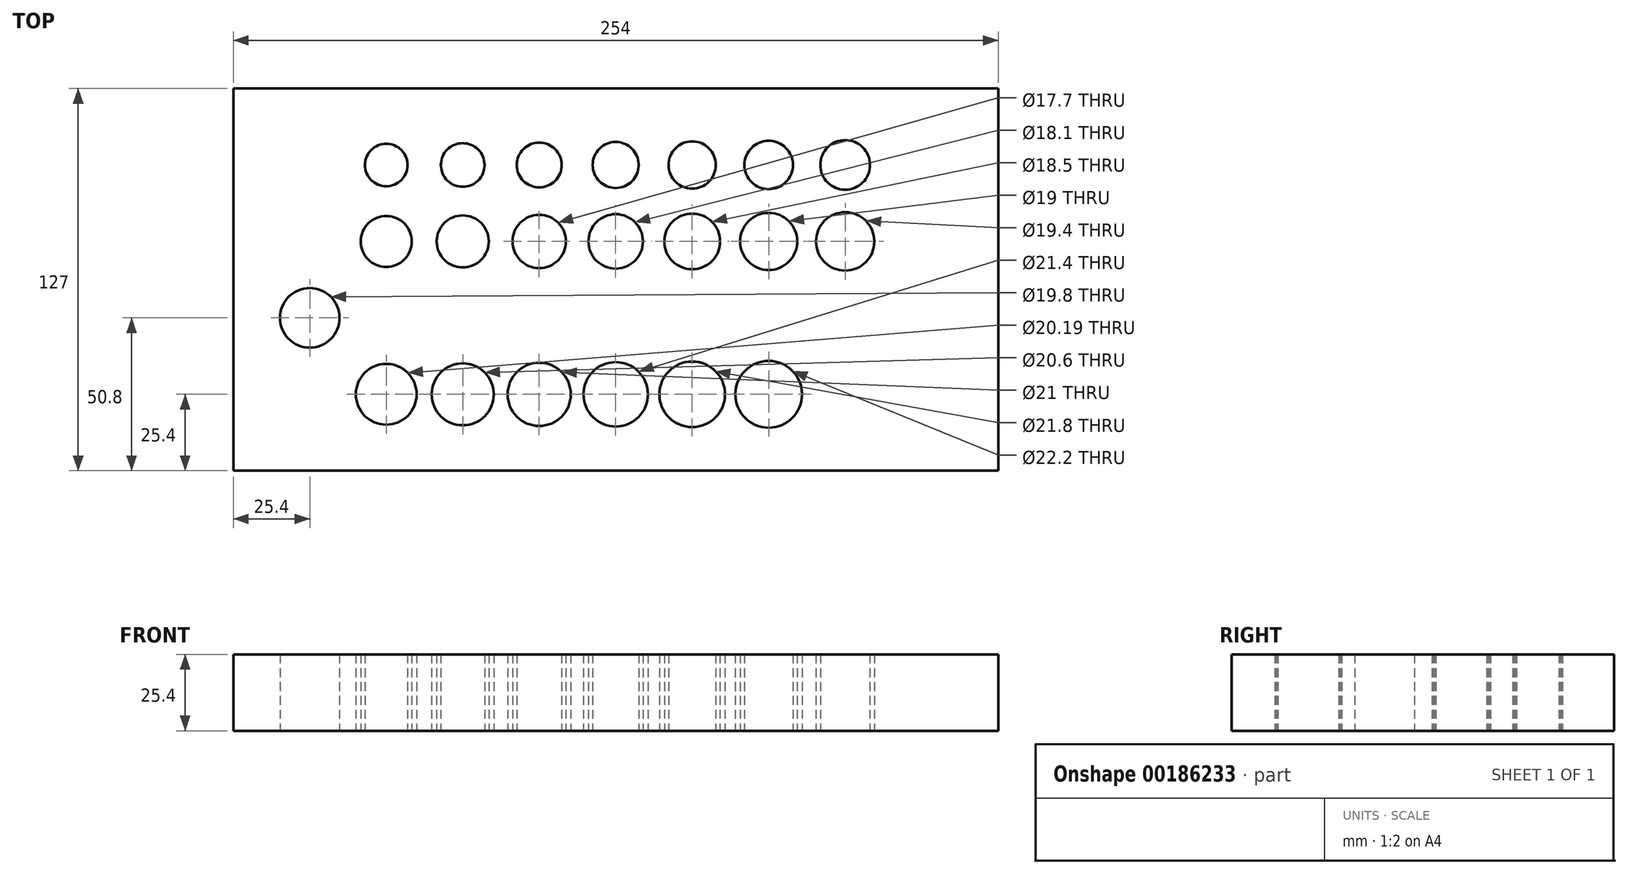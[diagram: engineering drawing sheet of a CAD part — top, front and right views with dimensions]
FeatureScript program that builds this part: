
annotation { "Feature Type Name" : "Feature", "Feature Type Description" : "" }
export const myFeature = defineFeature(function(context is Context, id is Id, definition is map)
    precondition{}
    {
        {
            var Q0;
            Q0=qCreatedBy(makeId("Top.planeOp"),FACE);
            var sketch = newSketch(context, id + "F0", { "sketchPlane" : qUnion([Q0])});
            skLineSegment(sketch, "E0.bottom", {"start": v(-127, 63.5) * mm, "end": v(127, 63.5) * mm});
            skLineSegment(sketch, "E0.top", {"start": v(-127, -63.5) * mm, "end": v(127, -63.5) * mm});
            skLineSegment(sketch, "E0.left", {"start": v(-127, 63.5) * mm, "end": v(-127, -63.5) * mm});
            skLineSegment(sketch, "E0.right", {"start": v(127, 63.5) * mm, "end": v(127, -63.5) * mm});
            skPoint(sketch, "E0.middle", {"position": v(0, 0) * mm});
            skPoint(sketch, "E1", {"position": v(-127, 38.1) * mm});
            skPoint(sketch, "E2", {"position": v(-127, 12.7) * mm});
            skPoint(sketch, "E3", {"position": v(-127, -12.7) * mm});
            skPoint(sketch, "E4", {"position": v(-127, -38.1) * mm});
            skPoint(sketch, "E5", {"position": v(-101.6, 63.5) * mm});
            skPoint(sketch, "E6", {"position": v(-76.2, 63.5) * mm});
            skPoint(sketch, "E7", {"position": v(-50.8, 63.5) * mm});
            skPoint(sketch, "E8", {"position": v(-25.4, 63.5) * mm});
            skPoint(sketch, "E9", {"position": v(0, 63.5) * mm});
            skPoint(sketch, "E10", {"position": v(25.4, 63.5) * mm});
            skPoint(sketch, "E11", {"position": v(50.8, 63.5) * mm});
            skPoint(sketch, "E12", {"position": v(76.2, 63.5) * mm});
            skPoint(sketch, "E13", {"position": v(101.6, 63.5) * mm});
            skPoint(sketch, "E14", {"position": v(-101.6, 38.1) * mm});
            skPoint(sketch, "E15", {"position": v(-76.2, 38.1) * mm});
            skPoint(sketch, "E16", {"position": v(-50.8, 38.1) * mm});
            skPoint(sketch, "E17", {"position": v(-25.4, 38.1) * mm});
            skPoint(sketch, "E18", {"position": v(0, 38.1) * mm});
            skPoint(sketch, "E19", {"position": v(25.4, 38.1) * mm});
            skPoint(sketch, "E20", {"position": v(50.8, 38.1) * mm});
            skPoint(sketch, "E21", {"position": v(76.2, 38.1) * mm});
            skPoint(sketch, "E22", {"position": v(101.6, 38.1) * mm});
            skPoint(sketch, "E23", {"position": v(-101.6, 12.7) * mm});
            skPoint(sketch, "E24", {"position": v(-76.2, 12.7) * mm});
            skPoint(sketch, "E25", {"position": v(-50.8, 12.7) * mm});
            skPoint(sketch, "E26", {"position": v(-25.4, 12.7) * mm});
            skPoint(sketch, "E27", {"position": v(0, 12.7) * mm});
            skPoint(sketch, "E28", {"position": v(25.4, 12.7) * mm});
            skPoint(sketch, "E29", {"position": v(50.8, 12.7) * mm});
            skPoint(sketch, "E30", {"position": v(76.2, 12.7) * mm});
            skPoint(sketch, "E31", {"position": v(101.6, 12.7) * mm});
            skPoint(sketch, "E32", {"position": v(-101.6, -12.7) * mm});
            skPoint(sketch, "E33", {"position": v(-76.2, -12.7) * mm});
            skPoint(sketch, "E34", {"position": v(-50.8, -12.7) * mm});
            skPoint(sketch, "E35", {"position": v(-25.4, -12.7) * mm});
            skPoint(sketch, "E36", {"position": v(0, -12.7) * mm});
            skPoint(sketch, "E37", {"position": v(25.4, -12.7) * mm});
            skPoint(sketch, "E38", {"position": v(50.8, -12.7) * mm});
            skPoint(sketch, "E39", {"position": v(76.2, -12.7) * mm});
            skPoint(sketch, "E40", {"position": v(101.6, -12.7) * mm});
            skPoint(sketch, "E41", {"position": v(-101.6, -38.1) * mm});
            skPoint(sketch, "E42", {"position": v(-76.2, -38.1) * mm});
            skPoint(sketch, "E43", {"position": v(-50.8, -38.1) * mm});
            skPoint(sketch, "E44", {"position": v(-25.4, -38.1) * mm});
            skPoint(sketch, "E45", {"position": v(0, -38.1) * mm});
            skPoint(sketch, "E46", {"position": v(25.4, -38.1) * mm});
            skPoint(sketch, "E47", {"position": v(50.8, -38.1) * mm});
            skPoint(sketch, "E48", {"position": v(76.2, -38.1) * mm});
            skPoint(sketch, "E49", {"position": v(101.6, -38.1) * mm});
            skCircle(sketch, "E50", {"center": v(-76.2, 38.1) * mm, "radius": 7.05 * mm});
            skCircle(sketch, "E51", {"center": v(-50.8, 38.1) * mm, "radius": 7.25 * mm});
            skCircle(sketch, "E52", {"center": v(-25.4, 38.1) * mm, "radius": 7.45 * mm});
            skCircle(sketch, "E53", {"center": v(0, 38.1) * mm, "radius": 7.65 * mm});
            skCircle(sketch, "E54", {"center": v(25.4, 38.1) * mm, "radius": 7.85 * mm});
            skCircle(sketch, "E55", {"center": v(50.8, 38.1) * mm, "radius": 8.05 * mm});
            skCircle(sketch, "E56", {"center": v(76.2, 38.1) * mm, "radius": 8.25 * mm});
            skCircle(sketch, "E57", {"center": v(-76.2, 12.7) * mm, "radius": 8.45 * mm});
            skCircle(sketch, "E58", {"center": v(-50.8, 12.7) * mm, "radius": 8.65 * mm});
            skCircle(sketch, "E59", {"center": v(-25.4, 12.7) * mm, "radius": 8.85 * mm});
            skCircle(sketch, "E60", {"center": v(0, 12.7) * mm, "radius": 9.05 * mm});
            skCircle(sketch, "E61", {"center": v(25.4, 12.7) * mm, "radius": 9.25 * mm});
            skCircle(sketch, "E62", {"center": v(50.8, 12.7) * mm, "radius": 9.5 * mm});
            skCircle(sketch, "E63", {"center": v(76.2, 12.7) * mm, "radius": 9.7 * mm});
            skCircle(sketch, "E64", {"center": v(0, -38.1) * mm, "radius": 10.7 * mm});
            skLineSegment(sketch, "E65", {"start": v(-76.2, 38.1) * mm, "end": v(-76.2, 50.06) * mm});
            skLineSegment(sketch, "E66.top", {"start": v(-71.64, 52.52) * mm, "end": v(-80.76, 52.52) * mm});
            skLineSegment(sketch, "E66.left", {"start": v(-71.64, 47.61) * mm, "end": v(-71.64, 52.52) * mm});
            skLineSegment(sketch, "E66.right", {"start": v(-80.76, 47.61) * mm, "end": v(-80.76, 52.52) * mm});
            skPoint(sketch, "E66.middle", {"position": v(-76.2, 50.06) * mm});
            skLineSegment(sketch, "E67.0.1.0", {"start": v(-71.64, 28.13) * mm, "end": v(-80.76, 28.13) * mm});
            skLineSegment(sketch, "E67.0.1.1", {"start": v(-71.64, 23.23) * mm, "end": v(-71.64, 28.13) * mm});
            skLineSegment(sketch, "E67.0.1.2", {"start": v(-71.64, 23.23) * mm, "end": v(-80.76, 23.23) * mm});
            skLineSegment(sketch, "E67.0.1.3", {"start": v(-80.76, 23.23) * mm, "end": v(-80.76, 28.13) * mm});
            skLineSegment(sketch, "E67.1.0.0", {"start": v(-46.24, 52.52) * mm, "end": v(-55.36, 52.52) * mm});
            skLineSegment(sketch, "E67.1.0.1", {"start": v(-46.24, 47.61) * mm, "end": v(-46.24, 52.52) * mm});
            skLineSegment(sketch, "E67.1.0.2", {"start": v(-46.24, 47.61) * mm, "end": v(-55.36, 47.61) * mm});
            skLineSegment(sketch, "E67.1.0.3", {"start": v(-55.36, 47.61) * mm, "end": v(-55.36, 52.52) * mm});
            skLineSegment(sketch, "E67.1.1.0", {"start": v(-46.24, 28.13) * mm, "end": v(-55.36, 28.13) * mm});
            skLineSegment(sketch, "E67.1.1.1", {"start": v(-46.24, 23.23) * mm, "end": v(-46.24, 28.13) * mm});
            skLineSegment(sketch, "E67.1.1.2", {"start": v(-46.24, 23.23) * mm, "end": v(-55.36, 23.23) * mm});
            skLineSegment(sketch, "E67.1.1.3", {"start": v(-55.36, 23.23) * mm, "end": v(-55.36, 28.13) * mm});
            skLineSegment(sketch, "E67.2.0.0", {"start": v(-20.84, 52.52) * mm, "end": v(-29.96, 52.52) * mm});
            skLineSegment(sketch, "E67.2.0.1", {"start": v(-20.84, 47.61) * mm, "end": v(-20.84, 52.52) * mm});
            skLineSegment(sketch, "E67.2.0.2", {"start": v(-20.84, 47.61) * mm, "end": v(-29.96, 47.61) * mm});
            skLineSegment(sketch, "E67.2.0.3", {"start": v(-29.96, 47.61) * mm, "end": v(-29.96, 52.52) * mm});
            skLineSegment(sketch, "E67.2.1.0", {"start": v(-20.84, 28.13) * mm, "end": v(-29.96, 28.13) * mm});
            skLineSegment(sketch, "E67.2.1.1", {"start": v(-20.84, 23.23) * mm, "end": v(-20.84, 28.13) * mm});
            skLineSegment(sketch, "E67.2.1.2", {"start": v(-20.84, 23.23) * mm, "end": v(-29.96, 23.23) * mm});
            skLineSegment(sketch, "E67.2.1.3", {"start": v(-29.96, 23.23) * mm, "end": v(-29.96, 28.13) * mm});
            skLineSegment(sketch, "E67.3.0.0", {"start": v(4.56, 52.52) * mm, "end": v(-4.56, 52.52) * mm});
            skLineSegment(sketch, "E67.3.0.1", {"start": v(4.56, 47.61) * mm, "end": v(4.56, 52.52) * mm});
            skLineSegment(sketch, "E67.3.0.2", {"start": v(4.56, 47.61) * mm, "end": v(-4.56, 47.61) * mm});
            skLineSegment(sketch, "E67.3.0.3", {"start": v(-4.56, 47.61) * mm, "end": v(-4.56, 52.52) * mm});
            skLineSegment(sketch, "E67.3.1.0", {"start": v(4.56, 28.13) * mm, "end": v(-4.56, 28.13) * mm});
            skLineSegment(sketch, "E67.3.1.1", {"start": v(4.56, 23.23) * mm, "end": v(4.56, 28.13) * mm});
            skLineSegment(sketch, "E67.3.1.2", {"start": v(4.56, 23.23) * mm, "end": v(-4.56, 23.23) * mm});
            skLineSegment(sketch, "E67.3.1.3", {"start": v(-4.56, 23.23) * mm, "end": v(-4.56, 28.13) * mm});
            skLineSegment(sketch, "E67.4.0.0", {"start": v(29.96, 52.52) * mm, "end": v(20.84, 52.52) * mm});
            skLineSegment(sketch, "E67.4.0.1", {"start": v(29.96, 47.61) * mm, "end": v(29.96, 52.52) * mm});
            skLineSegment(sketch, "E67.4.0.2", {"start": v(29.96, 47.61) * mm, "end": v(20.84, 47.61) * mm});
            skLineSegment(sketch, "E67.4.0.3", {"start": v(20.84, 47.61) * mm, "end": v(20.84, 52.52) * mm});
            skLineSegment(sketch, "E67.4.1.0", {"start": v(29.96, 28.13) * mm, "end": v(20.84, 28.13) * mm});
            skLineSegment(sketch, "E67.4.1.1", {"start": v(29.96, 23.23) * mm, "end": v(29.96, 28.13) * mm});
            skLineSegment(sketch, "E67.4.1.2", {"start": v(29.96, 23.23) * mm, "end": v(20.84, 23.23) * mm});
            skLineSegment(sketch, "E67.4.1.3", {"start": v(20.84, 23.23) * mm, "end": v(20.84, 28.13) * mm});
            skLineSegment(sketch, "E67.5.0.0", {"start": v(55.36, 52.52) * mm, "end": v(46.24, 52.52) * mm});
            skLineSegment(sketch, "E67.5.0.1", {"start": v(55.36, 47.61) * mm, "end": v(55.36, 52.52) * mm});
            skLineSegment(sketch, "E67.5.0.2", {"start": v(55.36, 47.61) * mm, "end": v(46.24, 47.61) * mm});
            skLineSegment(sketch, "E67.5.0.3", {"start": v(46.24, 47.61) * mm, "end": v(46.24, 52.52) * mm});
            skLineSegment(sketch, "E67.5.1.0", {"start": v(55.36, 28.13) * mm, "end": v(46.24, 28.13) * mm});
            skLineSegment(sketch, "E67.5.1.1", {"start": v(55.36, 23.23) * mm, "end": v(55.36, 28.13) * mm});
            skLineSegment(sketch, "E67.5.1.2", {"start": v(55.36, 23.23) * mm, "end": v(46.24, 23.23) * mm});
            skLineSegment(sketch, "E67.5.1.3", {"start": v(46.24, 23.23) * mm, "end": v(46.24, 28.13) * mm});
            skLineSegment(sketch, "E67.6.0.0", {"start": v(80.76, 52.52) * mm, "end": v(71.64, 52.52) * mm});
            skLineSegment(sketch, "E67.6.0.1", {"start": v(80.76, 47.61) * mm, "end": v(80.76, 52.52) * mm});
            skLineSegment(sketch, "E67.6.0.2", {"start": v(80.76, 47.61) * mm, "end": v(71.64, 47.61) * mm});
            skLineSegment(sketch, "E67.6.0.3", {"start": v(71.64, 47.61) * mm, "end": v(71.64, 52.52) * mm});
            skLineSegment(sketch, "E67.6.1.0", {"start": v(80.76, 28.13) * mm, "end": v(71.64, 28.13) * mm});
            skLineSegment(sketch, "E67.6.1.1", {"start": v(80.76, 23.23) * mm, "end": v(80.76, 28.13) * mm});
            skLineSegment(sketch, "E67.6.1.2", {"start": v(80.76, 23.23) * mm, "end": v(71.64, 23.23) * mm});
            skLineSegment(sketch, "E67.6.1.3", {"start": v(71.64, 23.23) * mm, "end": v(71.64, 28.13) * mm});
            skLineSegment(sketch, "E67.7.0.0", {"start": v(106.16, 52.52) * mm, "end": v(97.04, 52.52) * mm});
            skLineSegment(sketch, "E67.7.0.1", {"start": v(106.16, 47.61) * mm, "end": v(106.16, 52.52) * mm});
            skLineSegment(sketch, "E67.7.0.2", {"start": v(106.16, 47.61) * mm, "end": v(97.04, 47.61) * mm});
            skLineSegment(sketch, "E67.7.0.3", {"start": v(97.04, 47.61) * mm, "end": v(97.04, 52.52) * mm});
            skLineSegment(sketch, "E67.7.1.0", {"start": v(106.16, 28.13) * mm, "end": v(97.04, 28.13) * mm});
            skLineSegment(sketch, "E67.7.1.1", {"start": v(106.16, 23.23) * mm, "end": v(106.16, 28.13) * mm});
            skLineSegment(sketch, "E67.7.1.2", {"start": v(106.16, 23.23) * mm, "end": v(97.04, 23.23) * mm});
            skLineSegment(sketch, "E67.7.1.3", {"start": v(97.04, 23.23) * mm, "end": v(97.04, 28.13) * mm});
            skLineSegment(sketch, "E67.8.0.0", {"start": v(131.56, 52.52) * mm, "end": v(122.44, 52.52) * mm});
            skLineSegment(sketch, "E67.8.0.1", {"start": v(131.56, 47.61) * mm, "end": v(131.56, 52.52) * mm});
            skLineSegment(sketch, "E67.8.0.2", {"start": v(131.56, 47.61) * mm, "end": v(122.44, 47.61) * mm});
            skLineSegment(sketch, "E67.8.0.3", {"start": v(122.44, 47.61) * mm, "end": v(122.44, 52.52) * mm});
            skLineSegment(sketch, "E67.8.1.0", {"start": v(131.56, 28.13) * mm, "end": v(122.44, 28.13) * mm});
            skLineSegment(sketch, "E67.8.1.1", {"start": v(131.56, 23.23) * mm, "end": v(131.56, 28.13) * mm});
            skLineSegment(sketch, "E67.8.1.2", {"start": v(131.56, 23.23) * mm, "end": v(122.44, 23.23) * mm});
            skLineSegment(sketch, "E67.8.1.3", {"start": v(122.44, 23.23) * mm, "end": v(122.44, 28.13) * mm});
            skLineSegment(sketch, "E67.direction1", {"start": v(-80.76, 52.52) * mm, "end": v(-55.36, 52.52) * mm, "construction": true});
            skLineSegment(sketch, "E67.direction2", {"start": v(-80.76, 52.52) * mm, "end": v(-80.76, 28.13) * mm, "construction": true});
            skCircle(sketch, "E68", {"center": v(-101.6, -12.7) * mm, "radius": 9.9 * mm});
            skCircle(sketch, "E69", {"center": v(-76.2, -38.1) * mm, "radius": 10.1 * mm});
            skCircle(sketch, "E70", {"center": v(-50.8, -38.1) * mm, "radius": 10.3 * mm});
            skCircle(sketch, "E71", {"center": v(-25.4, -38.1) * mm, "radius": 10.5 * mm});
            skCircle(sketch, "E72", {"center": v(25.4, -38.1) * mm, "radius": 10.9 * mm});
            skCircle(sketch, "E73", {"center": v(50.8, -38.1) * mm, "radius": 11.1 * mm});
            skCircle(sketch, "E74", {"center": v(101.6, -38.1) * mm, "radius": 23.67 * mm});
            skLineSegment(sketch, "E75.0.1.0", {"start": v(-95.91, 0.1) * mm, "end": v(-105.03, 0.1) * mm});
            skLineSegment(sketch, "E75.0.1.1", {"start": v(-95.91, 0.1) * mm, "end": v(-95.91, 5) * mm});
            skLineSegment(sketch, "E75.0.1.2", {"start": v(-95.91, 5) * mm, "end": v(-105.03, 5) * mm});
            skLineSegment(sketch, "E75.direction1", {"start": v(-80.76, 23.23) * mm, "end": v(-55.36, 23.23) * mm, "construction": true});
            skLineSegment(sketch, "E75.direction2", {"start": v(-80.76, 23.23) * mm, "end": v(-105.03, 0.1) * mm, "construction": true});
            skLineSegment(sketch, "E76.0.1.0", {"start": v(-71.64, -19.37) * mm, "end": v(-80.76, -19.37) * mm});
            skLineSegment(sketch, "E76.0.1.1", {"start": v(-80.76, -24.27) * mm, "end": v(-80.76, -19.37) * mm});
            skLineSegment(sketch, "E76.0.1.2", {"start": v(-71.64, -24.27) * mm, "end": v(-71.64, -19.37) * mm});
            skLineSegment(sketch, "E76.0.1.3", {"start": v(-71.64, -24.27) * mm, "end": v(-80.76, -24.27) * mm});
            skLineSegment(sketch, "E76.1.1.0", {"start": v(-46.24, -19.37) * mm, "end": v(-55.36, -19.37) * mm});
            skLineSegment(sketch, "E76.1.1.1", {"start": v(-55.36, -24.27) * mm, "end": v(-55.36, -19.37) * mm});
            skLineSegment(sketch, "E76.1.1.2", {"start": v(-46.24, -24.27) * mm, "end": v(-46.24, -19.37) * mm});
            skLineSegment(sketch, "E76.1.1.3", {"start": v(-46.24, -24.27) * mm, "end": v(-55.36, -24.27) * mm});
            skLineSegment(sketch, "E76.2.1.0", {"start": v(-20.84, -19.37) * mm, "end": v(-29.96, -19.37) * mm});
            skLineSegment(sketch, "E76.2.1.1", {"start": v(-29.96, -24.27) * mm, "end": v(-29.96, -19.37) * mm});
            skLineSegment(sketch, "E76.2.1.2", {"start": v(-20.84, -24.27) * mm, "end": v(-20.84, -19.37) * mm});
            skLineSegment(sketch, "E76.2.1.3", {"start": v(-20.84, -24.27) * mm, "end": v(-29.96, -24.27) * mm});
            skLineSegment(sketch, "E76.3.1.0", {"start": v(4.56, -19.37) * mm, "end": v(-4.56, -19.37) * mm});
            skLineSegment(sketch, "E76.3.1.1", {"start": v(-4.56, -24.27) * mm, "end": v(-4.56, -19.37) * mm});
            skLineSegment(sketch, "E76.3.1.2", {"start": v(4.56, -24.27) * mm, "end": v(4.56, -19.37) * mm});
            skLineSegment(sketch, "E76.3.1.3", {"start": v(4.56, -24.27) * mm, "end": v(-4.56, -24.27) * mm});
            skLineSegment(sketch, "E76.4.1.0", {"start": v(29.96, -19.37) * mm, "end": v(20.84, -19.37) * mm});
            skLineSegment(sketch, "E76.4.1.1", {"start": v(20.84, -24.27) * mm, "end": v(20.84, -19.37) * mm});
            skLineSegment(sketch, "E76.4.1.2", {"start": v(29.96, -24.27) * mm, "end": v(29.96, -19.37) * mm});
            skLineSegment(sketch, "E76.4.1.3", {"start": v(29.96, -24.27) * mm, "end": v(20.84, -24.27) * mm});
            skLineSegment(sketch, "E76.5.1.0", {"start": v(55.36, -19.37) * mm, "end": v(46.24, -19.37) * mm});
            skLineSegment(sketch, "E76.5.1.1", {"start": v(46.24, -24.27) * mm, "end": v(46.24, -19.37) * mm});
            skLineSegment(sketch, "E76.5.1.2", {"start": v(55.36, -24.27) * mm, "end": v(55.36, -19.37) * mm});
            skLineSegment(sketch, "E76.5.1.3", {"start": v(55.36, -24.27) * mm, "end": v(46.24, -24.27) * mm});
            skLineSegment(sketch, "E76.direction1", {"start": v(-80.76, 28.13) * mm, "end": v(-55.36, 28.13) * mm, "construction": true});
            skLineSegment(sketch, "E76.direction2", {"start": v(-80.76, 28.13) * mm, "end": v(-80.76, -19.37) * mm, "construction": true});
            skSolve(sketch);
        }
        {
            var Q0;
            {var subQ5=sQuery(id+"F0.wireOp",EDGE,"E67.8.0.3");Q0=makeQuery(id+"F0.imprint","IMPRINT",FACE,{"disambiguationData":[TD([[makeQuery(id+"F0.imprint","IMPRINT",EDGE,{"derivedFrom":subQ5}),-1.0]])]});}
            var Q1;
            {var subQ5=sQuery(id+"F0.wireOp",EDGE,"E67.8.1.3");Q1=makeQuery(id+"F0.imprint","IMPRINT",FACE,{"disambiguationData":[TD([[makeQuery(id+"F0.imprint","IMPRINT",EDGE,{"derivedFrom":subQ5}),-1.0]])]});}
            var Q2;
            Q2=makeQuery(id+"F0.imprint","IMPRINT",FACE,{"disambiguationData":[TD([[makeQuery(id+"F0.imprint","IMPRINT",EDGE,{"derivedFrom":sQuery(id+"F0.wireOp",EDGE,"E67.1.0.0")}),1.0]])]});
            var Q3;
            Q3=makeQuery(id+"F0.imprint","IMPRINT",FACE,{"disambiguationData":[TD([[makeQuery(id+"F0.imprint","IMPRINT",EDGE,{"derivedFrom":sQuery(id+"F0.wireOp",EDGE,"E67.2.0.0")}),1.0]])]});
            var Q4;
            Q4=makeQuery(id+"F0.imprint","IMPRINT",FACE,{"disambiguationData":[TD([[makeQuery(id+"F0.imprint","IMPRINT",EDGE,{"derivedFrom":sQuery(id+"F0.wireOp",EDGE,"E67.3.0.0")}),1.0]])]});
            var Q5;
            Q5=makeQuery(id+"F0.imprint","IMPRINT",FACE,{"disambiguationData":[TD([[makeQuery(id+"F0.imprint","IMPRINT",EDGE,{"derivedFrom":sQuery(id+"F0.wireOp",EDGE,"E67.4.0.0")}),1.0]])]});
            var Q6;
            Q6=makeQuery(id+"F0.imprint","IMPRINT",FACE,{"disambiguationData":[TD([[makeQuery(id+"F0.imprint","IMPRINT",EDGE,{"derivedFrom":sQuery(id+"F0.wireOp",EDGE,"E67.0.1.0")}),1.0]])]});
            var Q7;
            Q7=makeQuery(id+"F0.imprint","IMPRINT",FACE,{"disambiguationData":[TD([[makeQuery(id+"F0.imprint","IMPRINT",EDGE,{"derivedFrom":sQuery(id+"F0.wireOp",EDGE,"E67.1.1.0")}),1.0]])]});
            var Q8;
            Q8=makeQuery(id+"F0.imprint","IMPRINT",FACE,{"disambiguationData":[TD([[makeQuery(id+"F0.imprint","IMPRINT",EDGE,{"derivedFrom":sQuery(id+"F0.wireOp",EDGE,"E67.2.1.0")}),1.0]])]});
            var Q9;
            Q9=makeQuery(id+"F0.imprint","IMPRINT",FACE,{"disambiguationData":[TD([[makeQuery(id+"F0.imprint","IMPRINT",EDGE,{"derivedFrom":sQuery(id+"F0.wireOp",EDGE,"E67.3.1.0")}),1.0]])]});
            var Q10;
            Q10=makeQuery(id+"F0.imprint","IMPRINT",FACE,{"disambiguationData":[TD([[makeQuery(id+"F0.imprint","IMPRINT",EDGE,{"derivedFrom":sQuery(id+"F0.wireOp",EDGE,"E67.4.1.0")}),1.0]])]});
            var Q11;
            Q11=makeQuery(id+"F0.imprint","IMPRINT",FACE,{"disambiguationData":[TD([[makeQuery(id+"F0.imprint","IMPRINT",EDGE,{"derivedFrom":sQuery(id+"F0.wireOp",EDGE,"E67.5.1.0")}),1.0]])]});
            var Q12;
            Q12=makeQuery(id+"F0.imprint","IMPRINT",FACE,{"disambiguationData":[TD([[makeQuery(id+"F0.imprint","IMPRINT",EDGE,{"derivedFrom":sQuery(id+"F0.wireOp",EDGE,"E67.5.0.0")}),1.0]])]});
            var Q13;
            Q13=makeQuery(id+"F0.imprint","IMPRINT",FACE,{"disambiguationData":[TD([[makeQuery(id+"F0.imprint","IMPRINT",EDGE,{"derivedFrom":sQuery(id+"F0.wireOp",EDGE,"E67.6.0.0")}),1.0]])]});
            var Q14;
            Q14=makeQuery(id+"F0.imprint","IMPRINT",FACE,{"disambiguationData":[TD([[makeQuery(id+"F0.imprint","IMPRINT",EDGE,{"derivedFrom":sQuery(id+"F0.wireOp",EDGE,"E67.7.0.0")}),1.0]])]});
            var Q15;
            Q15=makeQuery(id+"F0.imprint","IMPRINT",FACE,{"disambiguationData":[TD([[makeQuery(id+"F0.imprint","IMPRINT",EDGE,{"derivedFrom":sQuery(id+"F0.wireOp",EDGE,"E67.6.1.0")}),1.0]])]});
            var Q16;
            Q16=makeQuery(id+"F0.imprint","IMPRINT",FACE,{"disambiguationData":[TD([[makeQuery(id+"F0.imprint","IMPRINT",EDGE,{"derivedFrom":sQuery(id+"F0.wireOp",EDGE,"E76.0.1.0")}),1.0]])]});
            var Q17;
            Q17=makeQuery(id+"F0.imprint","IMPRINT",FACE,{"disambiguationData":[TD([[makeQuery(id+"F0.imprint","IMPRINT",EDGE,{"derivedFrom":sQuery(id+"F0.wireOp",EDGE,"E76.1.1.0")}),1.0]])]});
            var Q18;
            Q18=makeQuery(id+"F0.imprint","IMPRINT",FACE,{"disambiguationData":[TD([[makeQuery(id+"F0.imprint","IMPRINT",EDGE,{"derivedFrom":sQuery(id+"F0.wireOp",EDGE,"E76.2.1.0")}),1.0]])]});
            var Q19;
            Q19=makeQuery(id+"F0.imprint","IMPRINT",FACE,{"disambiguationData":[TD([[makeQuery(id+"F0.imprint","IMPRINT",EDGE,{"derivedFrom":sQuery(id+"F0.wireOp",EDGE,"E76.3.1.0")}),1.0]])]});
            var Q20;
            {var subQ11=sQuery(id+"F0.wireOp",EDGE,"E0.bottom");Q20=makeQuery(id+"F0.imprint","IMPRINT",FACE,{"disambiguationData":[TD([[makeQuery(id+"F0.imprint","IMPRINT",EDGE,{"derivedFrom":subQ11}),-1.0]])]});}
            var Q21;
            Q21=makeQuery(id+"F0.imprint","IMPRINT",FACE,{"disambiguationData":[TD([[makeQuery(id+"F0.imprint","IMPRINT",EDGE,{"derivedFrom":sQuery(id+"F0.wireOp",EDGE,"E76.5.1.0")}),1.0]])]});
            var Q22;
            Q22=makeQuery(id+"F0.imprint","IMPRINT",FACE,{"disambiguationData":[TD([[makeQuery(id+"F0.imprint","IMPRINT",EDGE,{"derivedFrom":sQuery(id+"F0.wireOp",EDGE,"E76.4.1.0")}),1.0]])]});
            var Q23;
            Q23=makeQuery(id+"F0.imprint","IMPRINT",FACE,{"disambiguationData":[TD([[makeQuery(id+"F0.imprint","IMPRINT",EDGE,{"derivedFrom":sQuery(id+"F0.wireOp",EDGE,"E67.7.1.0")}),1.0]])]});
            var Q24;
            Q24=makeQuery(id+"F0.imprint","IMPRINT",FACE,{"disambiguationData":[TD([[makeQuery(id+"F0.imprint","IMPRINT",EDGE,{"derivedFrom":sQuery(id+"F0.wireOp",EDGE,"E74")}),1.0]])]});
            extrude(context, id + "F1", {"entities" : qUnion([Q0, Q1, Q2, Q3, Q4, Q5, Q6, Q7, Q8, Q9, Q10, Q11, Q12, Q13, Q14, Q15, Q16, Q17, Q18, Q19, Q20, Q21, Q22, Q23, Q24]), "depth" : 25.4 * mm});
        }
    });
